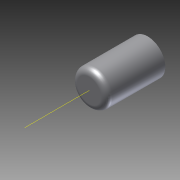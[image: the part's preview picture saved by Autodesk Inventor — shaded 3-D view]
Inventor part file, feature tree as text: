
AUTODESK INVENTOR PART (.ipt)
format: ipt  version: 2012 (Build 160160000, 160)  size: 85,504 bytes
history: native  units: in
note: dims shown in document units (in); Inventor stores cm internally (conversion verified against a paired STEP export)
features: extrude x1, fillet x1, other x1, sketch x1
ambient origin geometry x8: Origin, YZ Plane, XZ Plane, XY Plane, X Axis, Y Axis, Z Axis, Center Point
bodies: Solid1 (feature_tree)
feature tree (4):
  extrude  "Extrusion1"  Depth=0.1969in TaperAngle=0.0deg
  fillet  "Fillet1"  Radius=0.0197in
  other  "Work Axis1"
  sketch  "Sketch1"  dims[d0=0.1181in d1=0.1969in d2=0.0in d3=0.0197in]
